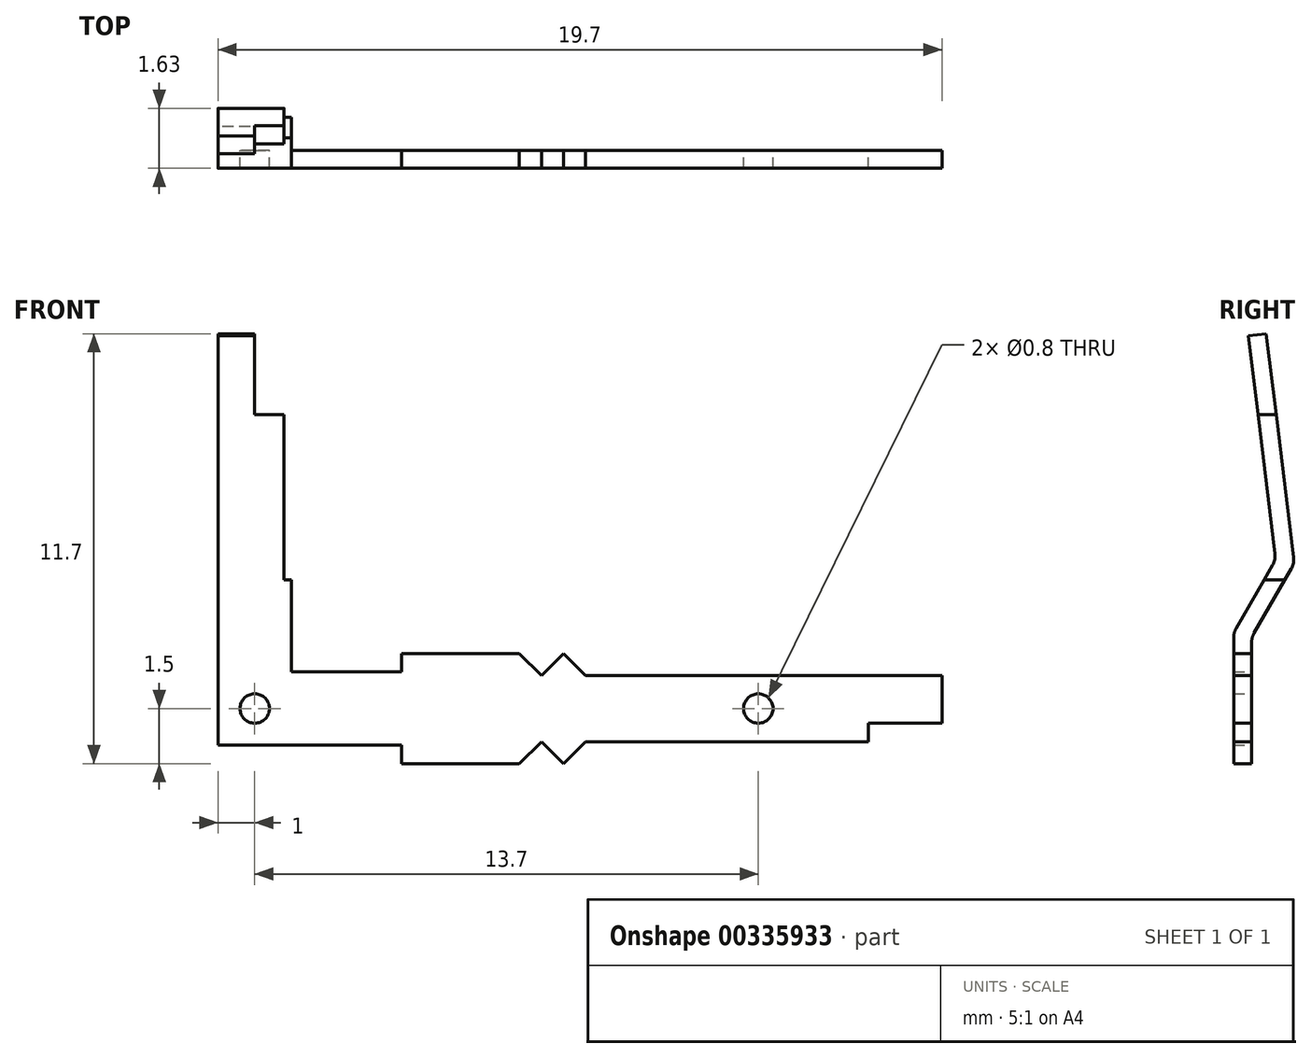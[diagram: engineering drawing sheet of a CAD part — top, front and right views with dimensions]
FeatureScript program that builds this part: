
annotation { "Feature Type Name" : "Feature", "Feature Type Description" : "" }
export const myFeature = defineFeature(function(context is Context, id is Id, definition is map)
    precondition{}
    {
        {
            var Q0;
            Q0=qCreatedBy(makeId("Front.planeOp"),FACE);
            var sketch = newSketch(context, id + "F0", { "sketchPlane" : qUnion([Q0])});
            skLineSegment(sketch, "E0", {"start": v(-1, 10.2) * mm, "end": v(-1, -1) * mm});
            skLineSegment(sketch, "E1", {"start": v(-1, -1) * mm, "end": v(4, -1) * mm});
            skLineSegment(sketch, "E2", {"start": v(4, -1) * mm, "end": v(4, -1.5) * mm});
            skLineSegment(sketch, "E3", {"start": v(4, -1.5) * mm, "end": v(7.2, -1.5) * mm});
            skLineSegment(sketch, "E4", {"start": v(7.2, -1.5) * mm, "end": v(7.8, -0.9) * mm});
            skLineSegment(sketch, "E5", {"start": v(7.8, -0.9) * mm, "end": v(8.4, -1.5) * mm});
            skLineSegment(sketch, "E6", {"start": v(8.4, -1.5) * mm, "end": v(9, -0.9) * mm});
            skLineSegment(sketch, "E7", {"start": v(9, -0.9) * mm, "end": v(16.7, -0.9) * mm});
            skLineSegment(sketch, "E8", {"start": v(16.7, -0.9) * mm, "end": v(16.7, -0.4) * mm});
            skLineSegment(sketch, "E9", {"start": v(16.7, -0.4) * mm, "end": v(18.7, -0.4) * mm});
            skLineSegment(sketch, "E10", {"start": v(18.7, -0.4) * mm, "end": v(18.7, 0.9) * mm});
            skLineSegment(sketch, "E11", {"start": v(18.7, 0.9) * mm, "end": v(9, 0.9) * mm});
            skLineSegment(sketch, "E12", {"start": v(9, 0.9) * mm, "end": v(8.4, 1.5) * mm});
            skLineSegment(sketch, "E13", {"start": v(8.4, 1.5) * mm, "end": v(7.8, 0.9) * mm});
            skLineSegment(sketch, "E14", {"start": v(7.8, 0.9) * mm, "end": v(7.2, 1.5) * mm});
            skLineSegment(sketch, "E15", {"start": v(7.2, 1.5) * mm, "end": v(4, 1.5) * mm});
            skLineSegment(sketch, "E16", {"start": v(4, 1.5) * mm, "end": v(4, 1) * mm});
            skLineSegment(sketch, "E17", {"start": v(4, 1) * mm, "end": v(1, 1) * mm});
            skLineSegment(sketch, "E18", {"start": v(1, 1) * mm, "end": v(1, 3.5) * mm});
            skLineSegment(sketch, "E19", {"start": v(0.8, 8) * mm, "end": v(0, 8) * mm});
            skLineSegment(sketch, "E20", {"start": v(0, 8) * mm, "end": v(0, 10.2) * mm});
            skLineSegment(sketch, "E21", {"start": v(0, 10.2) * mm, "end": v(-1, 10.2) * mm});
            skCircle(sketch, "E22", {"center": v(0, 0) * mm, "radius": 0.4 * mm});
            skLineSegment(sketch, "E23", {"start": v(0.8, 8) * mm, "end": v(0.8, 3.5) * mm});
            skLineSegment(sketch, "E24", {"start": v(0.8, 3.5) * mm, "end": v(1, 3.5) * mm});
            skCircle(sketch, "E25", {"center": v(13.7, 0) * mm, "radius": 0.4 * mm});
            skSolve(sketch);
        }
        {
            var Q0;
            Q0 = qSketchRegion(id + "F0", true);
            extrude(context, id + "F1", {"entities" : qUnion([Q0]), "endBound" : BoundingType.SYMMETRIC, "depth" : 5 * mm});
        }
        {
            var Q0;
            Q0=qCreatedBy(makeId("Right.planeOp"),FACE);
            var sketch = newSketch(context, id + "F2", { "sketchPlane" : qUnion([Q0])});
            skLineSegment(sketch, "E26.0", {"start": v(-2.5, 10.2) * mm, "end": v(2.5, 10.2) * mm, "construction": true});
            skLineSegment(sketch, "E27.0", {"start": v(-2.5, -1.5) * mm, "end": v(2.5, -1.5) * mm, "construction": true});
            skLineSegment(sketch, "E28", {"start": v(2.5, 10.2) * mm, "end": v(2.5, -1.5) * mm, "construction": true});
            skLineSegment(sketch, "E29", {"start": v(-2.5, 10.2) * mm, "end": v(-2.5, -1.5) * mm, "construction": true});
            skLineSegment(sketch, "E30", {"start": v(-0.4, -1.5) * mm, "end": v(-0.4, 2) * mm, "construction": true});
            skLineSegment(sketch, "E31", {"start": v(-0.4, 2) * mm, "end": v(0.76, 4) * mm, "construction": true});
            skLineSegment(sketch, "E32", {"start": v(0.76, 4) * mm, "end": v(0, 10.2) * mm, "construction": true});
            skLineSegment(sketch, "E33.0", {"start": v(1, 4.11) * mm, "end": v(0.25, 10.2) * mm});
            skLineSegment(sketch, "E33.1", {"start": v(-0.08, 2.05) * mm, "end": v(0.94, 3.8) * mm});
            skLineSegment(sketch, "E33.2", {"start": v(-0.14, -1.5) * mm, "end": v(-0.14, 1.8) * mm});
            skLineSegment(sketch, "E34.0", {"start": v(0.5, 4.22) * mm, "end": v(-0.23, 10.14) * mm});
            skLineSegment(sketch, "E34.1", {"start": v(-0.57, 2.18) * mm, "end": v(0.43, 3.9) * mm});
            skLineSegment(sketch, "E34.2", {"start": v(-0.63, -1.5) * mm, "end": v(-0.63, 1.93) * mm});
            skLineSegment(sketch, "E35", {"start": v(0.25, 10.2) * mm, "end": v(-0.23, 10.14) * mm});
            skLineSegment(sketch, "E36", {"start": v(-0.14, -1.5) * mm, "end": v(-0.63, -1.5) * mm});
            skPoint(sketch, "E37.visualSharp", {"position": v(0.51, 4.05) * mm});
            skArc(sketch, "E37.filletArc", {"start": v(0.43, 3.9) * mm, "mid": v(0.49, 4.06) * mm, "end": v(0.5, 4.22) * mm});
            skPoint(sketch, "E38.visualSharp", {"position": v(-0.63, 2.06) * mm});
            skArc(sketch, "E38.filletArc", {"start": v(-0.57, 2.18) * mm, "mid": v(-0.62, 2.06) * mm, "end": v(-0.63, 1.93) * mm});
            skPoint(sketch, "E39.visualSharp", {"position": v(-0.14, 1.93) * mm});
            skArc(sketch, "E39.filletArc", {"start": v(-0.08, 2.05) * mm, "mid": v(-0.13, 1.93) * mm, "end": v(-0.14, 1.8) * mm});
            skPoint(sketch, "E40.visualSharp", {"position": v(1.02, 3.95) * mm});
            skArc(sketch, "E40.filletArc", {"start": v(0.94, 3.8) * mm, "mid": v(1, 3.95) * mm, "end": v(1, 4.11) * mm});
            skSolve(sketch);
        }
        {
            var Q0;
            Q0 = qSketchRegion(id + "F2", true);
            extrude(context, id + "F3", {"entities" : qUnion([Q0]), "operationType" : NewBodyOperationType.INTERSECT, "endBound" : BoundingType.SYMMETRIC, "depth" : 70 * mm});
        }
    });
